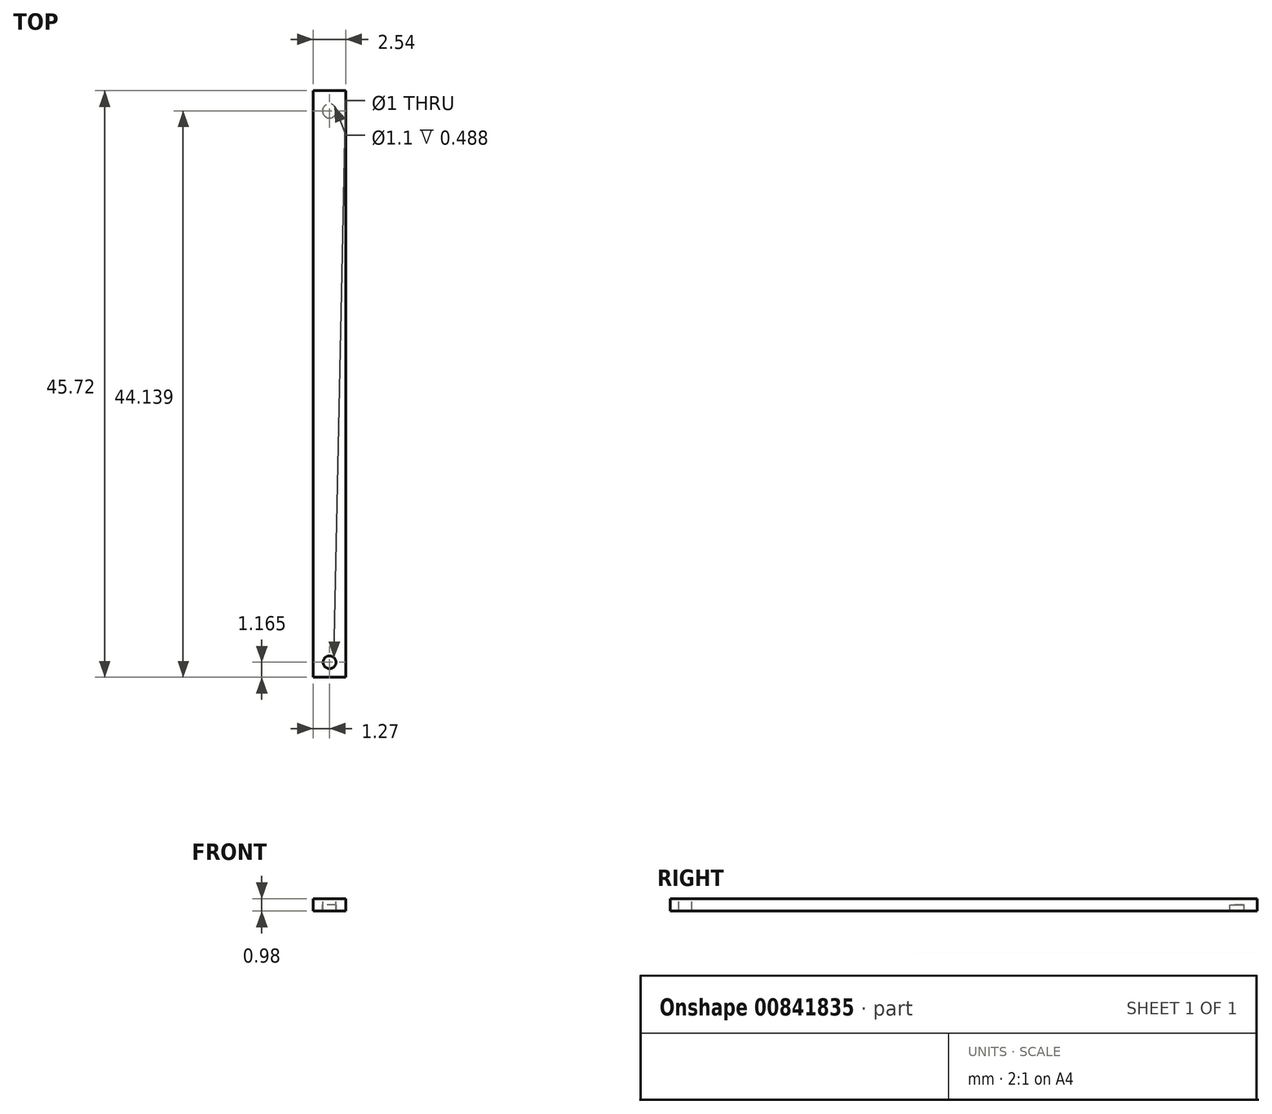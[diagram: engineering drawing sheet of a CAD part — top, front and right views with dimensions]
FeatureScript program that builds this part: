
annotation { "Feature Type Name" : "Feature", "Feature Type Description" : "" }
export const myFeature = defineFeature(function(context is Context, id is Id, definition is map)
    precondition{}
    {
        {
            var Q0;
            Q0=qCreatedBy(makeId("Front.planeOp"),FACE);
            var sketch = newSketch(context, id + "F0", { "sketchPlane" : qUnion([Q0])});
            skLineSegment(sketch, "E0.bottom", {"start": v(1.27, -0.49) * mm, "end": v(-1.27, -0.49) * mm});
            skLineSegment(sketch, "E0.top", {"start": v(1.27, 0.49) * mm, "end": v(-1.27, 0.49) * mm});
            skLineSegment(sketch, "E0.left", {"start": v(1.27, -0.49) * mm, "end": v(1.27, 0.49) * mm});
            skLineSegment(sketch, "E0.right", {"start": v(-1.27, -0.49) * mm, "end": v(-1.27, 0.49) * mm});
            skPoint(sketch, "E0.middle", {"position": v(0, 0) * mm});
            skSolve(sketch);
        }
        {
            var Q0;
            Q0=makeQuery(id+"F0.imprint","IMPRINT",FACE,{"disambiguationData":[TD([[makeQuery(id+"F0.imprint","IMPRINT",EDGE,{"derivedFrom":sQuery(id+"F0.wireOp",EDGE,"E0.bottom")}),-1.0]])]});
            extrude(context, id + "F1", {"entities" : qUnion([Q0]), "depth" : 45.72 * mm, "offsetDistance" : 25.4 * mm});
        }
        {
            var Q0;
            Q0=makeQuery(id+"F1.opExtrude","SWEPT_FACE",FACE,{"disambiguationData":[OSD([sQuery(id+"F0.wireOp",EDGE,"E0.top")])]});
            var sketch = newSketch(context, id + "F2", { "sketchPlane" : qUnion([Q0])});
            skCircle(sketch, "E1", {"center": v(0, -44.55) * mm, "radius": 0.5 * mm});
            skSolve(sketch);
        }
        {
            var Q0;
            Q0=makeQuery(id+"F2.imprint","IMPRINT",FACE,{"disambiguationData":[TD([[makeQuery(id+"F2.imprint","IMPRINT",EDGE,{"derivedFrom":sQuery(id+"F2.wireOp",EDGE,"E1")}),1.0]])]});
            extrude(context, id + "F3", {"entities" : qUnion([Q0]), "operationType" : NewBodyOperationType.REMOVE, "oppositeDirection" : true, "depth" : 25.4 * mm, "offsetDistance" : 25.4 * mm});
        }
        {
            var Q0;
            Q0=qCreatedBy(makeId("Top.planeOp"),FACE);
            var sketch = newSketch(context, id + "F4", { "sketchPlane" : qUnion([Q0])});
            skCircle(sketch, "E2", {"center": v(0, -1.58) * mm, "radius": 0.55 * mm});
            skSolve(sketch);
        }
        {
            var Q0;
            Q0 = qSketchRegion(id + "F4", true);
            extrude(context, id + "F5", {"entities" : qUnion([Q0]), "operationType" : NewBodyOperationType.REMOVE, "oppositeDirection" : true, "depth" : 50.8 * mm, "offsetDistance" : 25.4 * mm});
        }
    });
